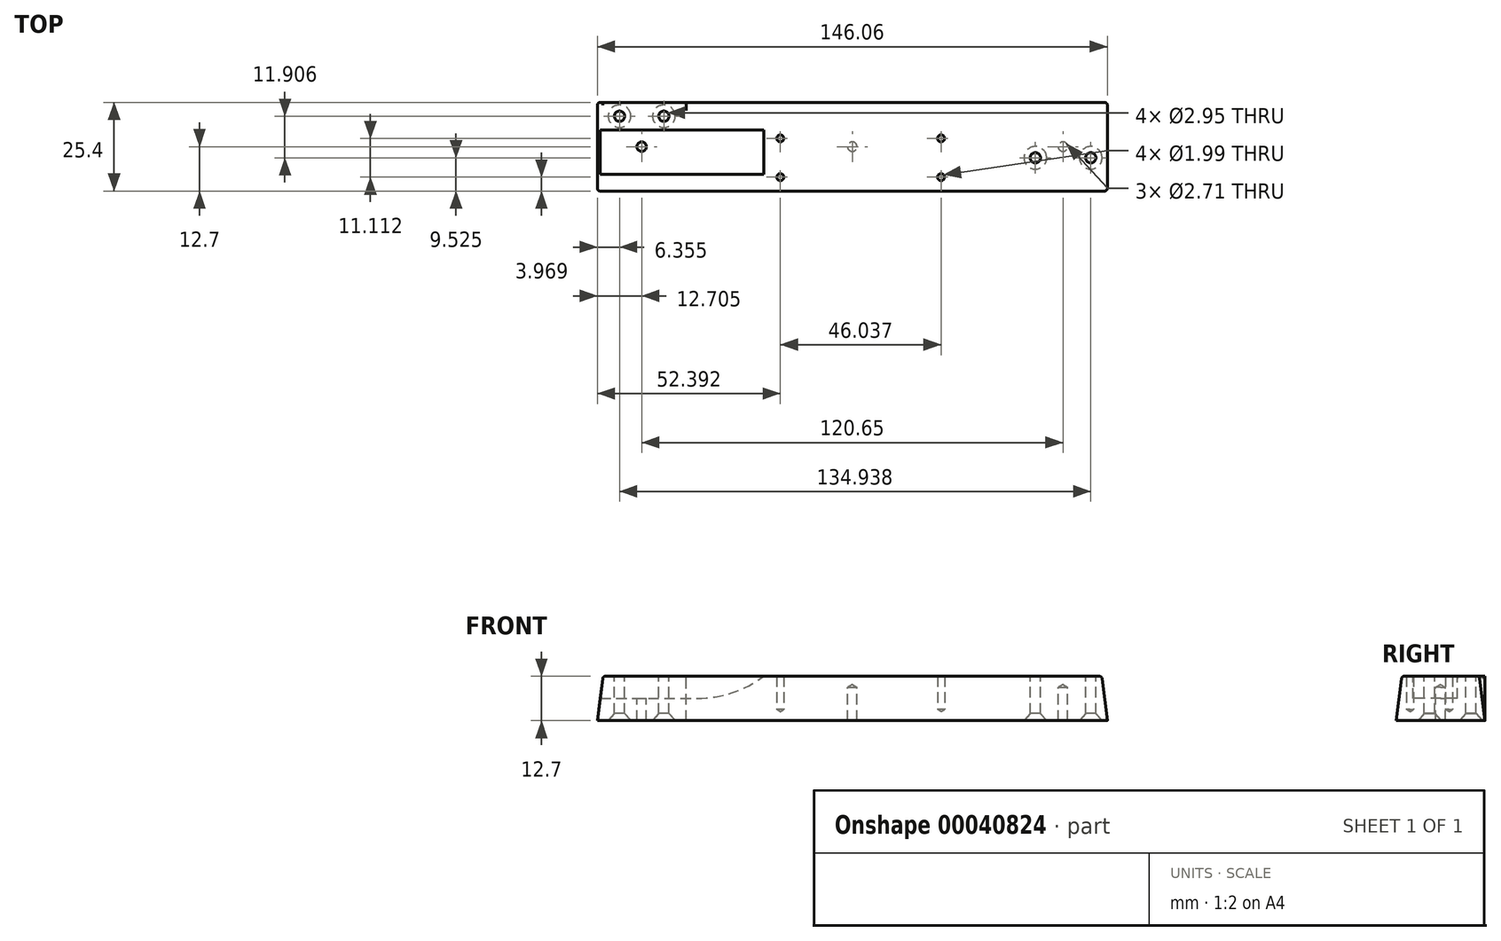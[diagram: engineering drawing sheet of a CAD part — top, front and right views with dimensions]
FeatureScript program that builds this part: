
annotation { "Feature Type Name" : "Feature", "Feature Type Description" : "" }
export const myFeature = defineFeature(function(context is Context, id is Id, definition is map)
    precondition{}
    {
        {
            var Q0;
            Q0=qCreatedBy(makeId("Top.planeOp"),FACE);
            var sketch = newSketch(context, id + "F0", { "sketchPlane" : qUnion([Q0])});
            skLineSegment(sketch, "E0.rect.bottom", {"start": v(-73.03, 12.7) * mm, "end": v(73.03, 12.7) * mm});
            skLineSegment(sketch, "E0.rect.top", {"start": v(-73.03, -12.7) * mm, "end": v(73.03, -12.7) * mm});
            skLineSegment(sketch, "E0.rect.left", {"start": v(-73.03, 12.7) * mm, "end": v(-73.03, -12.7) * mm});
            skLineSegment(sketch, "E0.rect.right", {"start": v(73.03, 12.7) * mm, "end": v(73.03, -12.7) * mm});
            skPoint(sketch, "E0.rect.middle", {"position": v(0, 0) * mm});
            skLineSegment(sketch, "E1", {"start": v(-73.03, 0) * mm, "end": v(73.03, 0) * mm, "construction": true});
            skLineSegment(sketch, "E2", {"start": v(-73.03, -8.73) * mm, "end": v(73.03, -8.73) * mm, "construction": true});
            skLineSegment(sketch, "E3", {"start": v(73.03, -3.18) * mm, "end": v(47.62, -3.17) * mm, "construction": true});
            skLineSegment(sketch, "E4", {"start": v(73.03, 2.38) * mm, "end": v(-73.03, 2.38) * mm, "construction": true});
            skLineSegment(sketch, "E5", {"start": v(-73.03, 8.73) * mm, "end": v(-47.62, 8.73) * mm, "construction": true});
            skPoint(sketch, "E6", {"position": v(-66.67, 8.73) * mm});
            skPoint(sketch, "E7", {"position": v(-53.98, 8.73) * mm});
            skPoint(sketch, "E8", {"position": v(-20.64, 2.38) * mm});
            skPoint(sketch, "E9", {"position": v(25.4, 2.38) * mm});
            skPoint(sketch, "E10", {"position": v(-60.33, 0) * mm});
            skPoint(sketch, "E11", {"position": v(60.33, 0) * mm});
            skPoint(sketch, "E12", {"position": v(52.39, -3.17) * mm});
            skPoint(sketch, "E13", {"position": v(68.26, -3.18) * mm});
            skPoint(sketch, "E14", {"position": v(25.4, -8.73) * mm});
            skPoint(sketch, "E15", {"position": v(-20.64, -8.73) * mm});
            skSolve(sketch);
        }
        {
            var Q0;
            Q0=makeQuery(id+"F0.imprint","IMPRINT",FACE,{"disambiguationData":[TD([[makeQuery(id+"F0.imprint","IMPRINT",EDGE,{"derivedFrom":sQuery(id+"F0.wireOp",EDGE,"E0.rect.bottom")}),-1.0]])]});
            extrude(context, id + "F1", {"entities" : qUnion([Q0]), "depth" : 12.7 * mm});
        }
        {
            var Q0;
            Q0=makeQuery(id+"F1.opExtrude","SWEPT_FACE",FACE,{"disambiguationData":[OSD([sQuery(id+"F0.wireOp",EDGE,"E0.rect.top")])]});
            cPlane(context, id + "F2", {"entities" : qUnion([Q0]), "cplaneType" : CPlaneType.OFFSET, "offset" : 4.76 * mm, "oppositeDirection" : true, "width" : 152.4 * mm, "height" : 152.4 * mm});
        }
        {
            var Q0;
            Q0=qCreatedBy(id+"F2.planeOp",FACE);
            var sketch = newSketch(context, id + "F3", { "sketchPlane" : qUnion([Q0])});
            skLineSegment(sketch, "E16.bottom", {"start": v(-73.03, 12.7) * mm, "end": v(-25.4, 12.7) * mm});
            skLineSegment(sketch, "E16.top", {"start": v(-73.03, 6.35) * mm, "end": v(-44.45, 6.35) * mm});
            skLineSegment(sketch, "E16.left", {"start": v(-73.03, 12.7) * mm, "end": v(-73.03, 6.35) * mm});
            skArc(sketch, "E17", {"start": v(-44.45, 6.35) * mm, "mid": v(-34.4, 7.98) * mm, "end": v(-25.4, 12.7) * mm});
            skSolve(sketch);
        }
        {
            var Q0;
            Q0=qCreatedBy(makeId("Front.planeOp"),FACE);
            var sketch = newSketch(context, id + "F4", { "sketchPlane" : qUnion([Q0])});
            skLineSegment(sketch, "E18.bottom", {"start": v(-73.03, 0) * mm, "end": v(-47.62, 0) * mm});
            skLineSegment(sketch, "E18.top", {"start": v(-71.44, 12.7) * mm, "end": v(-47.62, 12.7) * mm});
            skLineSegment(sketch, "E18.right", {"start": v(-47.62, 0) * mm, "end": v(-47.62, 12.7) * mm});
            skLineSegment(sketch, "E19", {"start": v(-71.44, 12.7) * mm, "end": v(-73.02, 0) * mm});
            skSolve(sketch);
        }
        {
            var Q0;
            Q0=makeQuery(id+"F1.opExtrude","CAP_EDGE",EDGE,{"disambiguationData":[OSD([sQuery(id+"F0.wireOp",EDGE,"E0.rect.left")])],"isStart":false});
            var Q1;
            Q1=makeQuery(id+"F1.opExtrude","CAP_EDGE",EDGE,{"disambiguationData":[OSD([sQuery(id+"F0.wireOp",EDGE,"E0.rect.top")])],"isStart":false});
            var Q2;
            Q2=makeQuery(id+"F1.opExtrude","CAP_EDGE",EDGE,{"disambiguationData":[OSD([sQuery(id+"F0.wireOp",EDGE,"E0.rect.right")])],"isStart":false});
            var Q3;
            Q3=makeQuery(id+"F1.opExtrude","CAP_EDGE",EDGE,{"disambiguationData":[OSD([sQuery(id+"F0.wireOp",EDGE,"E0.rect.bottom")])],"isStart":false});
            chamfer(context, id + "F5", {"entities" : qUnion([Q0, Q1, Q2, Q3]), "chamferType" : ChamferType.TWO_OFFSETS, "width1" : 1.59 * mm, "oppositeDirection" : false, "width2" : 12.7 * mm, "tangentPropagation" : true});
        }
        {
            var Q0;
            Q0=qSketchRegion(id+"F4",true);
            extrude(context, id + "F6", {"entities" : qUnion([Q0]), "operationType" : NewBodyOperationType.ADD, "oppositeDirection" : true, "depth" : 12.7 * mm});
        }
        {
            var Q0;
            Q0=sQuery(id+"F0.wireOp",VERTEX,"E6");
            var Q1;
            Q1=sQuery(id+"F0.wireOp",VERTEX,"E7");
            var Q2;
            Q2=sQuery(id+"F0.wireOp",VERTEX,"E12");
            var Q3;
            Q3=sQuery(id+"F0.wireOp",VERTEX,"E13");
            var Q4;
            Q4=makeQuery(id+"F1.opExtrude","SWEPT_BODY",BODY,{"disambiguationData":[OSD([sQuery(id+"F0.wireOp",EDGE,"E0.rect.bottom"),sQuery(id+"F0.wireOp",EDGE,"E0.rect.top"),sQuery(id+"F0.wireOp",EDGE,"E0.rect.left"),sQuery(id+"F0.wireOp",EDGE,"E0.rect.right")])]});
            hole(context, id + "F7", {"style" : HoleStyle.C_SINK, "holeDiameter" : 2.95 * mm, "cSinkDiameter" : 6.48 * mm, "endStyle" : HoleEndStyle.THROUGH, "oppositeDirection" : true, "locations" : qUnion([Q0, Q1, Q2, Q3]), "scope" : qUnion([Q4]), "cSinkAngle" : 82 * degree, "standardTappedOrClearance" : lookupTablePath({ "standard" : "ANSI", "fit" : "Close", "size" : "#4", "type" : "Clearance" }), "standardBlindInLast" : lookupTablePath({ "fit" : "Close", "standard" : "ANSI", "size" : "#4", "type" : "Clearance" }), "isTappedThrough" : true, "startStyle" : HoleStartStyle.PART});
        }
        {
            var Q0;
            Q0=sQuery(id+"F0.wireOp",VERTEX,"E10");
            var Q1;
            Q1=sQuery(id+"F0.wireOp",VERTEX,"E0.rect.middle");
            var Q2;
            Q2=sQuery(id+"F0.wireOp",VERTEX,"E11");
            var Q3;
            Q3=makeQuery(id+"F1.opExtrude","SWEPT_BODY",BODY,{"disambiguationData":[OSD([sQuery(id+"F0.wireOp",EDGE,"E0.rect.bottom"),sQuery(id+"F0.wireOp",EDGE,"E0.rect.top"),sQuery(id+"F0.wireOp",EDGE,"E0.rect.left"),sQuery(id+"F0.wireOp",EDGE,"E0.rect.right")])]});
            hole(context, id + "F8", {"style" : HoleStyle.SIMPLE, "holeDiameter" : 2.7 * mm, "endStyle" : HoleEndStyle.BLIND, "oppositeDirection" : true, "holeDepth" : 9.52 * mm, "locations" : qUnion([Q0, Q1, Q2]), "scope" : qUnion([Q3]), "standardTappedOrClearance" : lookupTablePath({ "standard" : "ANSI", "engagement" : "75%", "pitch" : "32 tpi", "size" : "#6", "type" : "Tapped" }), "standardBlindInLast" : lookupTablePath({ "standard" : "ANSI", "engagement" : "75%", "pitch" : "32 tpi", "size" : "#6", "type" : "Tapped" }), "majorDiameter" : 3.5 * mm, "startStyle" : HoleStartStyle.PART});
        }
        {
            var Q0;
            Q0=makeQuery(id+"F1.opExtrude","CAP_FACE",FACE,{"disambiguationData":[OSD([sQuery(id+"F0.wireOp",EDGE,"E0.rect.bottom"),sQuery(id+"F0.wireOp",EDGE,"E0.rect.top"),sQuery(id+"F0.wireOp",EDGE,"E0.rect.left"),sQuery(id+"F0.wireOp",EDGE,"E0.rect.right")])],"isStart":false});
            cPlane(context, id + "F9", {"entities" : qUnion([Q0]), "cplaneType" : CPlaneType.OFFSET, "offset" : 0 * mm, "width" : 152.4 * mm, "height" : 152.4 * mm});
        }
        {
            var Q0;
            Q0=qCreatedBy(id+"F9.planeOp",FACE);
            var sketch = newSketch(context, id + "F10", { "sketchPlane" : qUnion([Q0])});
            skLineSegment(sketch, "E20.rect.bottom", {"start": v(-73.03, 12.7) * mm, "end": v(73.03, 12.7) * mm});
            skLineSegment(sketch, "E20.rect.top", {"start": v(-73.02, -12.7) * mm, "end": v(73.03, -12.7) * mm});
            skLineSegment(sketch, "E20.rect.left", {"start": v(-73.02, 12.7) * mm, "end": v(-73.02, -12.7) * mm});
            skLineSegment(sketch, "E20.rect.right", {"start": v(73.03, 12.7) * mm, "end": v(73.03, -12.7) * mm});
            skPoint(sketch, "E20.rect.middle", {"position": v(0, 0) * mm});
            skLineSegment(sketch, "E21", {"start": v(-73.02, 0) * mm, "end": v(73.03, 0) * mm, "construction": true});
            skLineSegment(sketch, "E22", {"start": v(-73.02, -8.73) * mm, "end": v(73.03, -8.73) * mm, "construction": true});
            skLineSegment(sketch, "E23", {"start": v(73.03, -3.18) * mm, "end": v(47.63, -3.18) * mm, "construction": true});
            skLineSegment(sketch, "E24", {"start": v(73.03, 2.38) * mm, "end": v(-73.03, 2.38) * mm, "construction": true});
            skPoint(sketch, "E25", {"position": v(-66.67, 8.73) * mm});
            skPoint(sketch, "E26", {"position": v(-53.98, 8.73) * mm});
            skPoint(sketch, "E27", {"position": v(-20.64, 2.38) * mm});
            skPoint(sketch, "E28", {"position": v(25.4, 2.38) * mm});
            skPoint(sketch, "E29", {"position": v(-60.33, 0) * mm});
            skPoint(sketch, "E30", {"position": v(60.33, 0) * mm});
            skPoint(sketch, "E31", {"position": v(52.39, -3.18) * mm});
            skPoint(sketch, "E32", {"position": v(68.26, -3.18) * mm});
            skPoint(sketch, "E33", {"position": v(25.4, -8.73) * mm});
            skPoint(sketch, "E34", {"position": v(-20.64, -8.73) * mm});
            skSolve(sketch);
        }
        {
            var Q0;
            Q0=sQuery(id+"F10.wireOp",VERTEX,"E27");
            var Q1;
            Q1=sQuery(id+"F10.wireOp",VERTEX,"E28");
            var Q2;
            Q2=sQuery(id+"F10.wireOp",VERTEX,"E33");
            var Q3;
            Q3=sQuery(id+"F10.wireOp",VERTEX,"E34");
            var Q4;
            Q4=makeQuery(id+"F1.opExtrude","SWEPT_BODY",BODY,{"disambiguationData":[OSD([sQuery(id+"F0.wireOp",EDGE,"E0.rect.bottom"),sQuery(id+"F0.wireOp",EDGE,"E0.rect.top"),sQuery(id+"F0.wireOp",EDGE,"E0.rect.left"),sQuery(id+"F0.wireOp",EDGE,"E0.rect.right")])]});
            hole(context, id + "F11", {"style" : HoleStyle.SIMPLE, "holeDiameter" : 2 * mm, "endStyle" : HoleEndStyle.BLIND, "holeDepth" : 9.52 * mm, "locations" : qUnion([Q0, Q1, Q2, Q3]), "scope" : qUnion([Q4]), "standardTappedOrClearance" : lookupTablePath({ "standard" : "ANSI", "engagement" : "75%", "pitch" : "48 tpi", "size" : "#3", "type" : "Tapped" }), "standardBlindInLast" : lookupTablePath({ "standard" : "ANSI", "engagement" : "75%", "pitch" : "48 tpi", "size" : "#3", "type" : "Tapped" }), "majorDiameter" : 2.5 * mm, "startStyle" : HoleStartStyle.PART});
        }
        {
            var Q0;
            Q0=qSketchRegion(id+"F3",true);
            extrude(context, id + "F12", {"entities" : qUnion([Q0]), "operationType" : NewBodyOperationType.REMOVE, "oppositeDirection" : true, "depth" : 12.7 * mm});
        }
        {
            var Q0;
            {var subQ0=sQuery(id+"F0.wireOp",EDGE,"E0.rect.top");Q0=makeQuery(id+"F5.opChamfer","BLEND_EDGE",EDGE,{"blendedFrom":[makeQuery(id+"F1.opExtrude","CAP_EDGE",EDGE,{"disambiguationData":[OSD([subQ0])],"isStart":false}),makeQuery(id+"F1.opExtrude","CAP_FACE",FACE,{"disambiguationData":[OSD([sQuery(id+"F0.wireOp",EDGE,"E0.rect.bottom"),subQ0,sQuery(id+"F0.wireOp",EDGE,"E0.rect.left"),sQuery(id+"F0.wireOp",EDGE,"E0.rect.right")])],"isStart":false})],"blendedInto":[makeQuery(id+"F1.opExtrude","CAP_FACE",FACE,{"disambiguationData":[OSD([sQuery(id+"F0.wireOp",EDGE,"E0.rect.bottom"),subQ0,sQuery(id+"F0.wireOp",EDGE,"E0.rect.left"),sQuery(id+"F0.wireOp",EDGE,"E0.rect.right")])],"isStart":false})]});}
            var Q1;
            {var subQ0=sQuery(id+"F0.wireOp",EDGE,"E0.rect.right");Q1=makeQuery(id+"F5.opChamfer","BLEND_EDGE",EDGE,{"blendedFrom":[makeQuery(id+"F1.opExtrude","CAP_EDGE",EDGE,{"disambiguationData":[OSD([subQ0])],"isStart":false}),makeQuery(id+"F1.opExtrude","CAP_FACE",FACE,{"disambiguationData":[OSD([sQuery(id+"F0.wireOp",EDGE,"E0.rect.bottom"),sQuery(id+"F0.wireOp",EDGE,"E0.rect.top"),sQuery(id+"F0.wireOp",EDGE,"E0.rect.left"),subQ0])],"isStart":false})],"blendedInto":[makeQuery(id+"F1.opExtrude","CAP_FACE",FACE,{"disambiguationData":[OSD([sQuery(id+"F0.wireOp",EDGE,"E0.rect.bottom"),sQuery(id+"F0.wireOp",EDGE,"E0.rect.top"),sQuery(id+"F0.wireOp",EDGE,"E0.rect.left"),subQ0])],"isStart":false})]});}
            var Q2;
            {var subQ0=sQuery(id+"F0.wireOp",EDGE,"E0.rect.bottom");Q2=makeQuery(id+"F5.opChamfer","BLEND_EDGE",EDGE,{"blendedFrom":[makeQuery(id+"F1.opExtrude","CAP_EDGE",EDGE,{"disambiguationData":[OSD([subQ0])],"isStart":false}),makeQuery(id+"F1.opExtrude","CAP_FACE",FACE,{"disambiguationData":[OSD([subQ0,sQuery(id+"F0.wireOp",EDGE,"E0.rect.top"),sQuery(id+"F0.wireOp",EDGE,"E0.rect.left"),sQuery(id+"F0.wireOp",EDGE,"E0.rect.right")])],"isStart":false})],"blendedInto":[makeQuery(id+"F1.opExtrude","CAP_FACE",FACE,{"disambiguationData":[OSD([subQ0,sQuery(id+"F0.wireOp",EDGE,"E0.rect.top"),sQuery(id+"F0.wireOp",EDGE,"E0.rect.left"),sQuery(id+"F0.wireOp",EDGE,"E0.rect.right")])],"isStart":false})]});}
            var Q3;
            Q3=makeQuery(id+"F5.opChamfer","BLEND_EDGE",EDGE,{"blendedFrom":[makeQuery(id+"F1.opExtrude","CAP_EDGE",EDGE,{"disambiguationData":[OSD([sQuery(id+"F0.wireOp",EDGE,"E0.rect.top")])],"isStart":false}),makeQuery(id+"F1.opExtrude","CAP_EDGE",EDGE,{"disambiguationData":[OSD([sQuery(id+"F0.wireOp",EDGE,"E0.rect.left")])],"isStart":false})],"blendedInto":[]});
            var Q4;
            Q4=makeQuery(id+"F5.opChamfer","BLEND_EDGE",EDGE,{"blendedFrom":[makeQuery(id+"F1.opExtrude","CAP_EDGE",EDGE,{"disambiguationData":[OSD([sQuery(id+"F0.wireOp",EDGE,"E0.rect.top")])],"isStart":false}),makeQuery(id+"F1.opExtrude","CAP_EDGE",EDGE,{"disambiguationData":[OSD([sQuery(id+"F0.wireOp",EDGE,"E0.rect.right")])],"isStart":false})],"blendedInto":[]});
            var Q5;
            Q5=makeQuery(id+"F5.opChamfer","BLEND_EDGE",EDGE,{"blendedFrom":[makeQuery(id+"F1.opExtrude","CAP_EDGE",EDGE,{"disambiguationData":[OSD([sQuery(id+"F0.wireOp",EDGE,"E0.rect.bottom")])],"isStart":false}),makeQuery(id+"F1.opExtrude","CAP_EDGE",EDGE,{"disambiguationData":[OSD([sQuery(id+"F0.wireOp",EDGE,"E0.rect.right")])],"isStart":false})],"blendedInto":[]});
            var Q6;
            {var subQ0=sQuery(id+"F0.wireOp",EDGE,"E0.rect.left");var subQ1=sQuery(id+"F0.wireOp",EDGE,"E0.rect.top");var subQ2=makeQuery(id+"F1.opExtrude","CAP_FACE",FACE,{"disambiguationData":[OSD([sQuery(id+"F0.wireOp",EDGE,"E0.rect.bottom"),subQ1,subQ0,sQuery(id+"F0.wireOp",EDGE,"E0.rect.right")])],"isStart":false});var subQ3=sQuery(id+"F4.wireOp",EDGE,"E18.top");var subQ4=sQuery(id+"F4.wireOp",EDGE,"E19");Q6=makeQuery(id+"F12.boolean.opBoolean","SPLIT",EDGE,{"disambiguationData":[TD([makeQuery(id+"F5.opChamfer","BLEND_FACE",FACE,{"disambiguationData":[OSD([subQ1])]})])],"derivedFrom":makeQuery(id+"F6.boolean.opBoolean","MERGE",EDGE,{"derivedFrom":[makeQuery(id+"F5.opChamfer","BLEND_EDGE",EDGE,{"blendedFrom":[makeQuery(id+"F1.opExtrude","CAP_EDGE",EDGE,{"disambiguationData":[OSD([subQ0])],"isStart":false}),subQ2],"blendedInto":[subQ2]}),makeQuery(id+"F6.opExtrude","SWEPT_EDGE",EDGE,{"disambiguationData":[OSD([subQ3,subQ4])]})]})});}
            var Q7;
            {var subQ0=sQuery(id+"F0.wireOp",EDGE,"E0.rect.left");var subQ1=makeQuery(id+"F1.opExtrude","CAP_FACE",FACE,{"disambiguationData":[OSD([sQuery(id+"F0.wireOp",EDGE,"E0.rect.bottom"),sQuery(id+"F0.wireOp",EDGE,"E0.rect.top"),subQ0,sQuery(id+"F0.wireOp",EDGE,"E0.rect.right")])],"isStart":false});var subQ2=sQuery(id+"F4.wireOp",EDGE,"E18.top");var subQ3=sQuery(id+"F4.wireOp",EDGE,"E19");Q7=makeQuery(id+"F12.boolean.opBoolean","SPLIT",EDGE,{"disambiguationData":[TD([makeQuery(id+"F6.opExtrude","CAP_FACE",FACE,{"disambiguationData":[OSD([sQuery(id+"F4.wireOp",EDGE,"E18.bottom"),subQ2,sQuery(id+"F4.wireOp",EDGE,"E18.right"),subQ3])],"isStart":false})])],"derivedFrom":makeQuery(id+"F6.boolean.opBoolean","MERGE",EDGE,{"derivedFrom":[makeQuery(id+"F5.opChamfer","BLEND_EDGE",EDGE,{"blendedFrom":[makeQuery(id+"F1.opExtrude","CAP_EDGE",EDGE,{"disambiguationData":[OSD([subQ0])],"isStart":false}),subQ1],"blendedInto":[subQ1]}),makeQuery(id+"F6.opExtrude","SWEPT_EDGE",EDGE,{"disambiguationData":[OSD([subQ2,subQ3])]})]})});}
            var Q8;
            Q8=makeQuery(id+"F6.opExtrude","CAP_EDGE",EDGE,{"disambiguationData":[OSD([sQuery(id+"F4.wireOp",EDGE,"E19")])],"isStart":false});
            fillet(context, id + "F13", {"entities" : qUnion([Q0, Q1, Q2, Q3, Q4, Q5, Q6, Q7, Q8]), "radius" : 0.8 * mm, "tangentPropagation" : true, "allowEdgeOverflow" : false});
        }
    });
